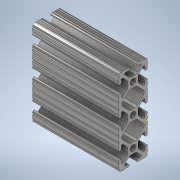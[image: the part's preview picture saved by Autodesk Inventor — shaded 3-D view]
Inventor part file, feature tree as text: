
AUTODESK INVENTOR PART (.ipt)
format: ipt  version: 2020 (Build 240168000, 168)  size: 371,200 bytes
history: native  units: in
note: dims shown in document units (in); Inventor stores cm internally (conversion verified against a paired STEP export)
features: sketch x2, extrude x1
ambient origin geometry x8: Origin, YZ Plane, XZ Plane, XY Plane, X Axis, Y Axis, Z Axis, Center Point
bodies: Solid1 (feature_tree)
feature tree (3):
  extrude  "Extrusion1"  [1 undecoded]
  sketch  "Sketch2"
  sketch  "Sketch1"  dims[d0=3.0in d1=0.0in]
note: 1 required parameter value undecoded (feature->parameter linkage not recoverable at this tier; creation-order binding heuristic only, values carry confidence <= 0.55)
